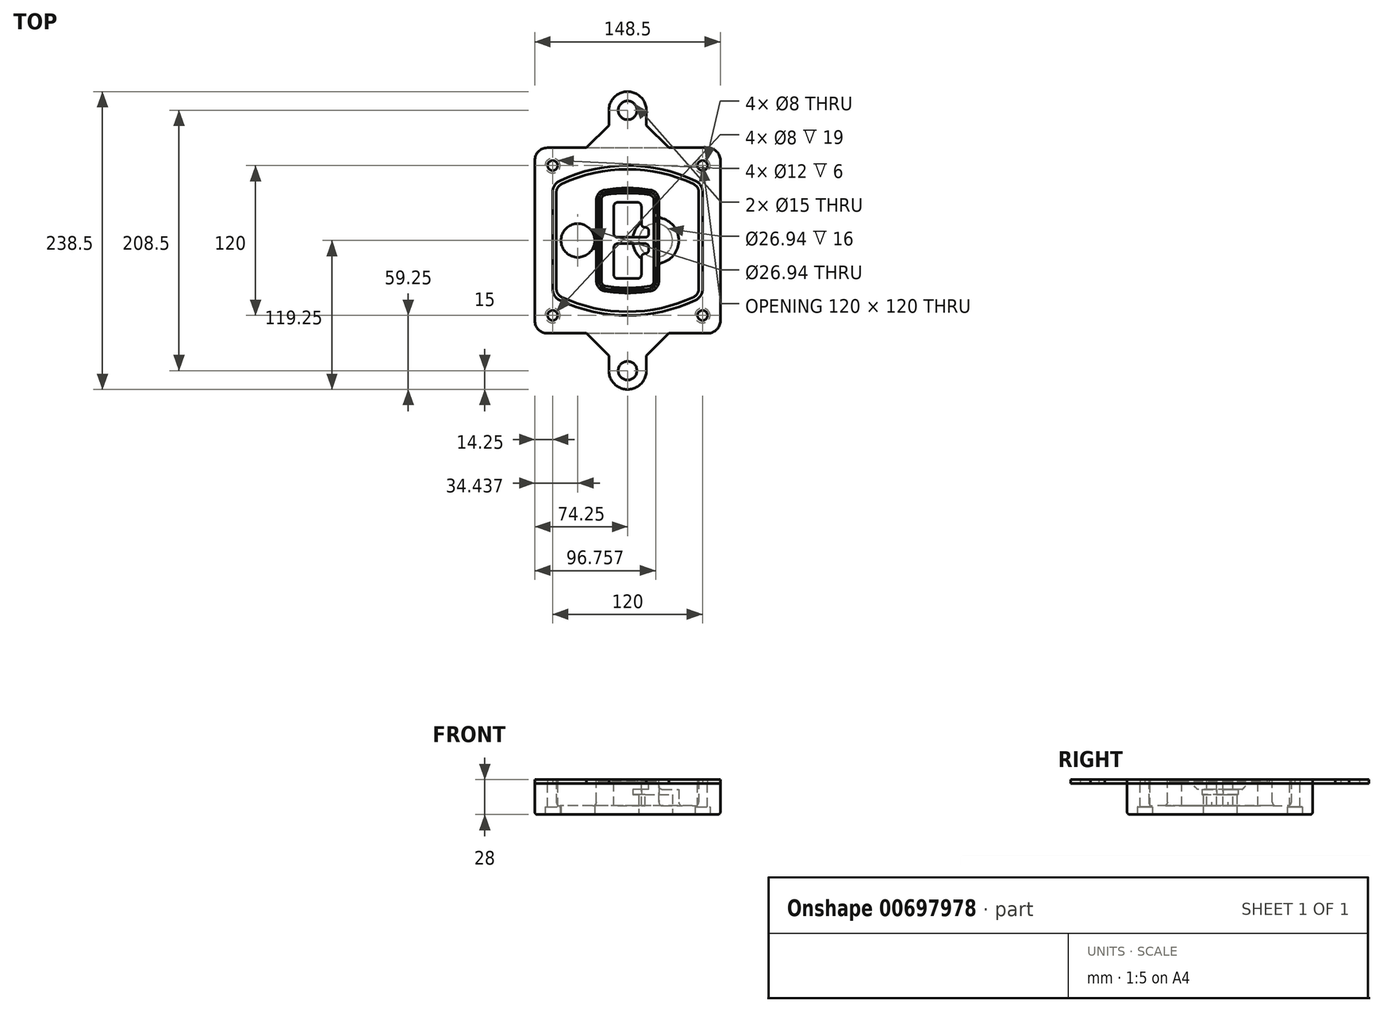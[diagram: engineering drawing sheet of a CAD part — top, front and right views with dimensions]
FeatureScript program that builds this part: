
annotation { "Feature Type Name" : "Feature", "Feature Type Description" : "" }
export const myFeature = defineFeature(function(context is Context, id is Id, definition is map)
    precondition{}
    {
        {
            var Q0;
            Q0=qCreatedBy(makeId("Top.planeOp"),FACE);
            var sketch = newSketch(context, id + "F0", { "sketchPlane" : qUnion([Q0])});
            skPoint(sketch, "E0.rect.middle", {"position": v(0, 0) * mm});
            skLineSegment(sketch, "E1.bottom", {"start": v(-64.25, -74.25) * mm, "end": v(64.25, -74.25) * mm});
            skLineSegment(sketch, "E1.top", {"start": v(-64.25, 74.25) * mm, "end": v(64.25, 74.25) * mm});
            skLineSegment(sketch, "E1.left", {"start": v(-74.25, -64.25) * mm, "end": v(-74.25, 64.25) * mm});
            skLineSegment(sketch, "E1.right", {"start": v(74.25, -64.25) * mm, "end": v(74.25, 64.25) * mm});
            skLineSegment(sketch, "E2", {"start": v(-74.25, 74.25) * mm, "end": v(74.25, -74.25) * mm, "construction": true});
            skLineSegment(sketch, "E3", {"start": v(74.25, 74.25) * mm, "end": v(-74.25, -74.25) * mm, "construction": true});
            skCircle(sketch, "E4", {"center": v(-60, 60) * mm, "radius": 4 * mm});
            skCircle(sketch, "E5", {"center": v(60, 60) * mm, "radius": 4 * mm});
            skCircle(sketch, "E6", {"center": v(60, -60) * mm, "radius": 4 * mm});
            skCircle(sketch, "E7", {"center": v(-60, -60) * mm, "radius": 4 * mm});
            skLineSegment(sketch, "E8", {"start": v(-60, 60) * mm, "end": v(60, 60) * mm, "construction": true});
            skLineSegment(sketch, "E9", {"start": v(60, 60) * mm, "end": v(60, -60) * mm, "construction": true});
            skLineSegment(sketch, "E10", {"start": v(60, -60) * mm, "end": v(-60, -60) * mm, "construction": true});
            skLineSegment(sketch, "E11", {"start": v(-60, -60) * mm, "end": v(-60, 60) * mm, "construction": true});
            skLineSegment(sketch, "E12", {"start": v(-60, 38.83) * mm, "end": v(-60, -38.83) * mm});
            skLineSegment(sketch, "E13", {"start": v(60, 38.83) * mm, "end": v(60, -38.83) * mm});
            skArc(sketch, "E14", {"start": v(54.26, 47.88) * mm, "mid": v(0, 60) * mm, "end": v(-54.26, 47.88) * mm});
            skArc(sketch, "E15", {"start": v(-54.26, -47.88) * mm, "mid": v(0, -60) * mm, "end": v(54.26, -47.88) * mm});
            skLineSegment(sketch, "E16", {"start": v(-60, 0) * mm, "end": v(60, 0) * mm, "construction": true});
            skPoint(sketch, "E17.visualSharp", {"position": v(-60, -45) * mm});
            skArc(sketch, "E17.filletArc", {"start": v(-60, -38.83) * mm, "mid": v(-58.44, -44.2) * mm, "end": v(-54.26, -47.88) * mm});
            skPoint(sketch, "E18.visualSharp", {"position": v(-60, 45) * mm});
            skArc(sketch, "E18.filletArc", {"start": v(-54.26, 47.88) * mm, "mid": v(-58.44, 44.2) * mm, "end": v(-60, 38.83) * mm});
            skPoint(sketch, "E19.visualSharp", {"position": v(60, 45) * mm});
            skArc(sketch, "E19.filletArc", {"start": v(60, 38.83) * mm, "mid": v(58.44, 44.2) * mm, "end": v(54.26, 47.88) * mm});
            skPoint(sketch, "E20.visualSharp", {"position": v(60, -45) * mm});
            skArc(sketch, "E20.filletArc", {"start": v(54.26, -47.88) * mm, "mid": v(58.44, -44.2) * mm, "end": v(60, -38.83) * mm});
            skPoint(sketch, "E21.visualSharp", {"position": v(-74.25, 74.25) * mm});
            skArc(sketch, "E21.filletArc", {"start": v(-64.25, 74.25) * mm, "mid": v(-71.32, 71.32) * mm, "end": v(-74.25, 64.25) * mm});
            skPoint(sketch, "E22.visualSharp", {"position": v(74.25, 74.25) * mm});
            skArc(sketch, "E22.filletArc", {"start": v(74.25, 64.25) * mm, "mid": v(71.32, 71.32) * mm, "end": v(64.25, 74.25) * mm});
            skPoint(sketch, "E23.visualSharp", {"position": v(74.25, -74.25) * mm});
            skArc(sketch, "E23.filletArc", {"start": v(64.25, -74.25) * mm, "mid": v(71.32, -71.32) * mm, "end": v(74.25, -64.25) * mm});
            skPoint(sketch, "E24.visualSharp", {"position": v(-74.25, -74.25) * mm});
            skArc(sketch, "E24.filletArc", {"start": v(-74.25, -64.25) * mm, "mid": v(-71.32, -71.32) * mm, "end": v(-64.25, -74.25) * mm});
            skArc(sketch, "E25.0", {"start": v(57, 38.83) * mm, "mid": v(55.9, 42.58) * mm, "end": v(52.98, 45.17) * mm});
            skLineSegment(sketch, "E25.1", {"start": v(57, 38.83) * mm, "end": v(57, -38.83) * mm});
            skArc(sketch, "E25.2", {"start": v(52.98, -45.17) * mm, "mid": v(55.9, -42.58) * mm, "end": v(57, -38.83) * mm});
            skArc(sketch, "E25.3", {"start": v(-52.98, -45.17) * mm, "mid": v(0, -57) * mm, "end": v(52.98, -45.17) * mm});
            skArc(sketch, "E25.4", {"start": v(-57, -38.83) * mm, "mid": v(-55.9, -42.58) * mm, "end": v(-52.98, -45.17) * mm});
            skArc(sketch, "E25.5", {"start": v(52.98, 45.17) * mm, "mid": v(0, 57) * mm, "end": v(-52.98, 45.17) * mm});
            skLineSegment(sketch, "E25.6", {"start": v(-57, 38.83) * mm, "end": v(-57, -38.83) * mm});
            skArc(sketch, "E25.7", {"start": v(-52.98, 45.17) * mm, "mid": v(-55.9, 42.58) * mm, "end": v(-57, 38.83) * mm});
            skArc(sketch, "E26.0", {"start": v(-55.96, 51.5) * mm, "mid": v(-61.82, 46.33) * mm, "end": v(-64, 38.83) * mm});
            skArc(sketch, "E26.1", {"start": v(55.96, 51.5) * mm, "mid": v(0, 64) * mm, "end": v(-55.96, 51.5) * mm});
            skArc(sketch, "E26.2", {"start": v(64, 38.83) * mm, "mid": v(61.82, 46.33) * mm, "end": v(55.96, 51.5) * mm});
            skLineSegment(sketch, "E26.3", {"start": v(64, 38.83) * mm, "end": v(64, -38.83) * mm});
            skArc(sketch, "E26.4", {"start": v(55.96, -51.5) * mm, "mid": v(61.82, -46.33) * mm, "end": v(64, -38.83) * mm});
            skLineSegment(sketch, "E26.5", {"start": v(-64, 38.83) * mm, "end": v(-64, -38.83) * mm});
            skArc(sketch, "E26.6", {"start": v(-55.96, -51.5) * mm, "mid": v(0, -64) * mm, "end": v(55.96, -51.5) * mm});
            skArc(sketch, "E26.7", {"start": v(-64, -38.83) * mm, "mid": v(-61.82, -46.33) * mm, "end": v(-55.96, -51.5) * mm});
            skSolve(sketch);
        }
        {
            var Q0;
            Q0=makeQuery(id+"F0.imprint","IMPRINT",FACE,{"disambiguationData":[TD([[makeQuery(id+"F0.imprint","IMPRINT",EDGE,{"derivedFrom":sQuery(id+"F0.wireOp",EDGE,"E1.bottom")}),1.0]])]});
            var Q1;
            Q1=makeQuery(id+"F0.imprint","IMPRINT",FACE,{"disambiguationData":[TD([[makeQuery(id+"F0.imprint","IMPRINT",EDGE,{"derivedFrom":sQuery(id+"F0.wireOp",EDGE,"E12")}),1.0]])]});
            var Q2;
            Q2=makeQuery(id+"F0.imprint","IMPRINT",FACE,{"disambiguationData":[TD([[makeQuery(id+"F0.imprint","IMPRINT",EDGE,{"derivedFrom":sQuery(id+"F0.wireOp",EDGE,"E25.0")}),1.0]])]});
            var Q3;
            Q3=makeQuery(id+"F0.imprint","IMPRINT",FACE,{"disambiguationData":[TD([[makeQuery(id+"F0.imprint","IMPRINT",EDGE,{"derivedFrom":sQuery(id+"F0.wireOp",EDGE,"E12")}),-1.0]])]});
            extrude(context, id + "F1", {"entities" : qUnion([Q0, Q1, Q2, Q3]), "oppositeDirection" : true, "depth" : 25 * mm});
        }
        {
            var Q0;
            Q0=makeQuery(id+"F0.imprint","IMPRINT",FACE,{"disambiguationData":[TD([[makeQuery(id+"F0.imprint","IMPRINT",EDGE,{"derivedFrom":sQuery(id+"F0.wireOp",EDGE,"E12")}),1.0]])]});
            extrude(context, id + "F2", {"entities" : qUnion([Q0]), "operationType" : NewBodyOperationType.ADD, "depth" : 3 * mm});
        }
        {
            var Q0;
            Q0=makeQuery(id+"F0.imprint","IMPRINT",FACE,{"disambiguationData":[TD([[makeQuery(id+"F0.imprint","IMPRINT",EDGE,{"derivedFrom":sQuery(id+"F0.wireOp",EDGE,"E25.0")}),1.0]])]});
            extrude(context, id + "F3", {"entities" : qUnion([Q0]), "operationType" : NewBodyOperationType.REMOVE, "oppositeDirection" : true, "depth" : 18 * mm});
        }
        {
            var Q0;
            Q0=makeQuery(id+"F2.opExtrude","CAP_FACE",FACE,{"disambiguationData":[OSD([sQuery(id+"F0.wireOp",EDGE,"E12"),sQuery(id+"F0.wireOp",EDGE,"E13"),sQuery(id+"F0.wireOp",EDGE,"E14"),sQuery(id+"F0.wireOp",EDGE,"E15"),sQuery(id+"F0.wireOp",EDGE,"E17.filletArc"),sQuery(id+"F0.wireOp",EDGE,"E18.filletArc"),sQuery(id+"F0.wireOp",EDGE,"E19.filletArc"),sQuery(id+"F0.wireOp",EDGE,"E20.filletArc"),sQuery(id+"F0.wireOp",EDGE,"E25.0"),sQuery(id+"F0.wireOp",EDGE,"E25.1"),sQuery(id+"F0.wireOp",EDGE,"E25.2"),sQuery(id+"F0.wireOp",EDGE,"E25.3"),sQuery(id+"F0.wireOp",EDGE,"E25.4"),sQuery(id+"F0.wireOp",EDGE,"E25.5"),sQuery(id+"F0.wireOp",EDGE,"E25.6"),sQuery(id+"F0.wireOp",EDGE,"E25.7")])],"isStart":false});
            var sketch = newSketch(context, id + "F4", { "sketchPlane" : qUnion([Q0])});
            skArc(sketch, "E27.0", {"start": v(-18.34, -40.45) * mm, "mid": v(0, -42) * mm, "end": v(18.34, -40.45) * mm});
            skArc(sketch, "E28.0", {"start": v(18.34, 40.45) * mm, "mid": v(0, 42) * mm, "end": v(-18.34, 40.45) * mm});
            skLineSegment(sketch, "E29", {"start": v(-25, 32.57) * mm, "end": v(-25, -32.57) * mm});
            skLineSegment(sketch, "E30", {"start": v(25, 32.57) * mm, "end": v(25, -32.57) * mm});
            skLineSegment(sketch, "E31", {"start": v(-25, 39.1) * mm, "end": v(25, 39.1) * mm, "construction": true});
            skLineSegment(sketch, "E32", {"start": v(-25, -39.1) * mm, "end": v(25, -39.1) * mm, "construction": true});
            skPoint(sketch, "E33.visualSharp", {"position": v(-25, 39.1) * mm});
            skArc(sketch, "E33.filletArc", {"start": v(-18.34, 40.45) * mm, "mid": v(-23.11, 37.73) * mm, "end": v(-25, 32.57) * mm});
            skPoint(sketch, "E34.visualSharp", {"position": v(25, 39.1) * mm});
            skArc(sketch, "E34.filletArc", {"start": v(25, 32.57) * mm, "mid": v(23.11, 37.73) * mm, "end": v(18.34, 40.45) * mm});
            skPoint(sketch, "E35.visualSharp", {"position": v(25, -39.1) * mm});
            skArc(sketch, "E35.filletArc", {"start": v(18.34, -40.45) * mm, "mid": v(23.11, -37.73) * mm, "end": v(25, -32.57) * mm});
            skPoint(sketch, "E36.visualSharp", {"position": v(-25, -39.1) * mm});
            skArc(sketch, "E36.filletArc", {"start": v(-25, -32.57) * mm, "mid": v(-23.11, -37.73) * mm, "end": v(-18.34, -40.45) * mm});
            skArc(sketch, "E37.0", {"start": v(52.98, 45.17) * mm, "mid": v(0, 57) * mm, "end": v(-52.98, 45.17) * mm});
            skArc(sketch, "E37.1", {"start": v(-52.98, 45.17) * mm, "mid": v(-55.9, 42.58) * mm, "end": v(-57, 38.83) * mm});
            skLineSegment(sketch, "E37.2", {"start": v(-57, 38.83) * mm, "end": v(-57, -38.83) * mm});
            skArc(sketch, "E37.3", {"start": v(-57, -38.83) * mm, "mid": v(-55.9, -42.58) * mm, "end": v(-52.98, -45.17) * mm});
            skArc(sketch, "E37.4", {"start": v(-52.98, -45.17) * mm, "mid": v(0, -57) * mm, "end": v(52.98, -45.17) * mm});
            skArc(sketch, "E37.5", {"start": v(52.98, -45.17) * mm, "mid": v(55.9, -42.58) * mm, "end": v(57, -38.83) * mm});
            skLineSegment(sketch, "E37.6", {"start": v(57, 38.83) * mm, "end": v(57, -38.83) * mm});
            skArc(sketch, "E37.7", {"start": v(57, 38.83) * mm, "mid": v(55.9, 42.58) * mm, "end": v(52.98, 45.17) * mm});
            skLineSegment(sketch, "E38.0", {"start": v(23, 32.57) * mm, "end": v(23, -32.57) * mm});
            skArc(sketch, "E38.1", {"start": v(18, -38.48) * mm, "mid": v(21.58, -36.44) * mm, "end": v(23, -32.57) * mm});
            skArc(sketch, "E38.2", {"start": v(-18, -38.48) * mm, "mid": v(0, -40) * mm, "end": v(18, -38.48) * mm});
            skArc(sketch, "E38.3", {"start": v(-23, -32.57) * mm, "mid": v(-21.58, -36.44) * mm, "end": v(-18, -38.48) * mm});
            skLineSegment(sketch, "E38.4", {"start": v(-23, 32.57) * mm, "end": v(-23, -32.57) * mm});
            skArc(sketch, "E38.5", {"start": v(23, 32.57) * mm, "mid": v(21.58, 36.44) * mm, "end": v(18, 38.48) * mm});
            skArc(sketch, "E38.6", {"start": v(-18, 38.48) * mm, "mid": v(-21.58, 36.44) * mm, "end": v(-23, 32.57) * mm});
            skArc(sketch, "E38.7", {"start": v(18, 38.48) * mm, "mid": v(0, 40) * mm, "end": v(-18, 38.48) * mm});
            skArc(sketch, "E39.0", {"start": v(21, 32.57) * mm, "mid": v(20.06, 35.15) * mm, "end": v(17.67, 36.5) * mm});
            skLineSegment(sketch, "E39.1", {"start": v(21, 32.57) * mm, "end": v(21, -32.57) * mm});
            skArc(sketch, "E39.2", {"start": v(17.67, -36.5) * mm, "mid": v(20.06, -35.15) * mm, "end": v(21, -32.57) * mm});
            skArc(sketch, "E39.3", {"start": v(-17.67, -36.5) * mm, "mid": v(0, -38) * mm, "end": v(17.67, -36.5) * mm});
            skArc(sketch, "E39.4", {"start": v(-21, -32.57) * mm, "mid": v(-20.06, -35.15) * mm, "end": v(-17.67, -36.5) * mm});
            skArc(sketch, "E39.5", {"start": v(17.67, 36.5) * mm, "mid": v(0, 38) * mm, "end": v(-17.67, 36.5) * mm});
            skLineSegment(sketch, "E39.6", {"start": v(-21, 32.57) * mm, "end": v(-21, -32.57) * mm});
            skArc(sketch, "E39.7", {"start": v(-17.67, 36.5) * mm, "mid": v(-20.06, 35.15) * mm, "end": v(-21, 32.57) * mm});
            skLineSegment(sketch, "E40", {"start": v(-25, 0) * mm, "end": v(25, 0) * mm, "construction": true});
            skLineSegment(sketch, "E41", {"start": v(-11, 5.5) * mm, "end": v(-11, 27.5) * mm});
            skLineSegment(sketch, "E42", {"start": v(-8, 30.5) * mm, "end": v(8, 30.5) * mm});
            skLineSegment(sketch, "E43", {"start": v(11, 27.5) * mm, "end": v(11, 13.5) * mm});
            skLineSegment(sketch, "E44", {"start": v(14, 10.5) * mm, "end": v(14, 10.5) * mm});
            skLineSegment(sketch, "E45", {"start": v(17, 7.5) * mm, "end": v(17, 5.5) * mm});
            skLineSegment(sketch, "E46", {"start": v(14, 2.5) * mm, "end": v(-8, 2.5) * mm});
            skPoint(sketch, "E47.visualSharp", {"position": v(-11, 30.5) * mm});
            skArc(sketch, "E47.filletArc", {"start": v(-8, 30.5) * mm, "mid": v(-10.12, 29.62) * mm, "end": v(-11, 27.5) * mm});
            skPoint(sketch, "E48.visualSharp", {"position": v(11, 30.5) * mm});
            skArc(sketch, "E48.filletArc", {"start": v(11, 27.5) * mm, "mid": v(10.12, 29.62) * mm, "end": v(8, 30.5) * mm});
            skPoint(sketch, "E49.visualSharp", {"position": v(11, 10.5) * mm});
            skArc(sketch, "E49.filletArc", {"start": v(11, 13.5) * mm, "mid": v(11.88, 11.38) * mm, "end": v(14, 10.5) * mm});
            skPoint(sketch, "E50.visualSharp", {"position": v(17, 10.5) * mm});
            skArc(sketch, "E50.filletArc", {"start": v(17, 7.5) * mm, "mid": v(16.12, 9.62) * mm, "end": v(14, 10.5) * mm});
            skPoint(sketch, "E51.visualSharp", {"position": v(17, 2.5) * mm});
            skArc(sketch, "E51.filletArc", {"start": v(14, 2.5) * mm, "mid": v(16.12, 3.38) * mm, "end": v(17, 5.5) * mm});
            skPoint(sketch, "E52.visualSharp", {"position": v(-11, 2.5) * mm});
            skArc(sketch, "E52.filletArc", {"start": v(-11, 5.5) * mm, "mid": v(-10.12, 3.38) * mm, "end": v(-8, 2.5) * mm});
            skLineSegment(sketch, "E53.0.MirrorCS", {"start": v(14, -2.5) * mm, "end": v(-8, -2.5) * mm});
            skArc(sketch, "E54.0.MirrorCS", {"start": v(-11, -5.5) * mm, "mid": v(-10.12, -3.38) * mm, "end": v(-8, -2.5) * mm});
            skLineSegment(sketch, "E55.0.MirrorCS", {"start": v(-11, -5.5) * mm, "end": v(-11, -27.5) * mm});
            skArc(sketch, "E56.0.MirrorCS", {"start": v(-8, -30.5) * mm, "mid": v(-10.12, -29.62) * mm, "end": v(-11, -27.5) * mm});
            skLineSegment(sketch, "E57.0.MirrorCS", {"start": v(-8, -30.5) * mm, "end": v(8, -30.5) * mm});
            skArc(sketch, "E58.0.MirrorCS", {"start": v(11, -27.5) * mm, "mid": v(10.12, -29.62) * mm, "end": v(8, -30.5) * mm});
            skLineSegment(sketch, "E59.0.MirrorCS", {"start": v(11, -27.5) * mm, "end": v(11, -13.5) * mm});
            skArc(sketch, "E60.0.MirrorCS", {"start": v(11, -13.5) * mm, "mid": v(11.88, -11.38) * mm, "end": v(14, -10.5) * mm});
            skArc(sketch, "E61.0.MirrorCS", {"start": v(17, -7.5) * mm, "mid": v(16.12, -9.62) * mm, "end": v(14, -10.5) * mm});
            skLineSegment(sketch, "E62.0.MirrorCS", {"start": v(17, -7.5) * mm, "end": v(17, -5.5) * mm});
            skArc(sketch, "E63.0.MirrorCS", {"start": v(14, -2.5) * mm, "mid": v(16.12, -3.38) * mm, "end": v(17, -5.5) * mm});
            skSolve(sketch);
        }
        {
            var Q0;
            Q0=makeQuery(id+"F4.imprint","IMPRINT",FACE,{"disambiguationData":[TD([[makeQuery(id+"F4.imprint","IMPRINT",EDGE,{"derivedFrom":sQuery(id+"F4.wireOp",EDGE,"E27.0")}),1.0]])]});
            var Q1;
            Q1=makeQuery(id+"F4.imprint","IMPRINT",FACE,{"disambiguationData":[TD([[makeQuery(id+"F4.imprint","IMPRINT",EDGE,{"derivedFrom":sQuery(id+"F4.wireOp",EDGE,"E38.0")}),-1.0]])]});
            var Q2;
            Q2=makeQuery(id+"F4.imprint","IMPRINT",FACE,{"disambiguationData":[TD([[makeQuery(id+"F4.imprint","IMPRINT",EDGE,{"derivedFrom":sQuery(id+"F4.wireOp",EDGE,"E39.0")}),1.0]])]});
            extrude(context, id + "F5", {"entities" : qUnion([Q0, Q1, Q2]), "operationType" : NewBodyOperationType.ADD, "endBound" : BoundingType.UP_TO_NEXT, "oppositeDirection" : true, "depth" : 25 * mm});
        }
        {
            var Q0;
            Q0=makeQuery(id+"F4.imprint","IMPRINT",FACE,{"disambiguationData":[TD([[makeQuery(id+"F4.imprint","IMPRINT",EDGE,{"derivedFrom":sQuery(id+"F4.wireOp",EDGE,"E38.0")}),-1.0]])]});
            extrude(context, id + "F6", {"entities" : qUnion([Q0]), "operationType" : NewBodyOperationType.REMOVE, "oppositeDirection" : true, "depth" : 2 * mm});
        }
        {
            var Q0;
            Q0=makeQuery(id+"F1.opExtrude","CAP_FACE",FACE,{"disambiguationData":[OSD([sQuery(id+"F0.wireOp",EDGE,"E1.bottom"),sQuery(id+"F0.wireOp",EDGE,"E1.top"),sQuery(id+"F0.wireOp",EDGE,"E1.left"),sQuery(id+"F0.wireOp",EDGE,"E1.right"),sQuery(id+"F0.wireOp",EDGE,"E4"),sQuery(id+"F0.wireOp",EDGE,"E5"),sQuery(id+"F0.wireOp",EDGE,"E6"),sQuery(id+"F0.wireOp",EDGE,"E7"),sQuery(id+"F0.wireOp",EDGE,"E21.filletArc"),sQuery(id+"F0.wireOp",EDGE,"E22.filletArc"),sQuery(id+"F0.wireOp",EDGE,"E23.filletArc"),sQuery(id+"F0.wireOp",EDGE,"E24.filletArc")])],"isStart":false});
            var sketch = newSketch(context, id + "F7", { "sketchPlane" : qUnion([Q0])});
            skCircle(sketch, "E64", {"center": v(22.5, 0) * mm, "radius": 13.47 * mm});
            skCircle(sketch, "E65", {"center": v(-39.81, 0) * mm, "radius": 13.47 * mm});
            skLineSegment(sketch, "E66", {"start": v(74.25, 0) * mm, "end": v(-74.25, 0) * mm});
            skCircle(sketch, "E67", {"center": v(22.5, 0) * mm, "radius": 18.47 * mm});
            skCircle(sketch, "E68", {"center": v(60, -60) * mm, "radius": 6 * mm});
            skCircle(sketch, "E69", {"center": v(-60, -60) * mm, "radius": 6 * mm});
            skCircle(sketch, "E70", {"center": v(-60, 60) * mm, "radius": 6 * mm});
            skCircle(sketch, "E71", {"center": v(60, 60) * mm, "radius": 6 * mm});
            skSolve(sketch);
        }
        {
            var Q0;
            {var subQ1=sQuery(id+"F7.wireOp",EDGE,"E66");var subQ4=sQuery(id+"F7.wireOp",EDGE,"E64");var subQ6=makeQuery(id+"F7.imprint","INTERSECT",VERTEX,{"disambiguationData":[OD(0.0)],"derivedFrom":[subQ4,subQ1]});Q0=makeQuery(id+"F7.imprint","IMPRINT",FACE,{"disambiguationData":[TD([[makeQuery(id+"F7.imprint","IMPRINT",EDGE,{"disambiguationData":[TD([[subQ6,-1.0]])],"derivedFrom":subQ4}),-1.0]])]});}
            var Q1;
            {var subQ0=sQuery(id+"F7.wireOp",EDGE,"E66");var subQ1=sQuery(id+"F7.wireOp",EDGE,"E64");var subQ3=makeQuery(id+"F7.imprint","INTERSECT",VERTEX,{"disambiguationData":[OD(0.0)],"derivedFrom":[subQ1,subQ0]});Q1=makeQuery(id+"F7.imprint","IMPRINT",FACE,{"disambiguationData":[TD([[makeQuery(id+"F7.imprint","IMPRINT",EDGE,{"disambiguationData":[TD([[subQ3,-1.0]])],"derivedFrom":subQ1}),1.0]])]});}
            var Q2;
            {var subQ0=sQuery(id+"F7.wireOp",EDGE,"E66");var subQ1=sQuery(id+"F7.wireOp",EDGE,"E64");var subQ3=makeQuery(id+"F7.imprint","INTERSECT",VERTEX,{"disambiguationData":[OD(0.0)],"derivedFrom":[subQ1,subQ0]});Q2=makeQuery(id+"F7.imprint","IMPRINT",FACE,{"disambiguationData":[TD([[makeQuery(id+"F7.imprint","IMPRINT",EDGE,{"disambiguationData":[TD([[subQ3,1.0]])],"derivedFrom":subQ1}),1.0]])]});}
            var Q3;
            {var subQ1=sQuery(id+"F7.wireOp",EDGE,"E66");var subQ4=sQuery(id+"F7.wireOp",EDGE,"E64");var subQ6=makeQuery(id+"F7.imprint","INTERSECT",VERTEX,{"disambiguationData":[OD(0.0)],"derivedFrom":[subQ4,subQ1]});Q3=makeQuery(id+"F7.imprint","IMPRINT",FACE,{"disambiguationData":[TD([[makeQuery(id+"F7.imprint","IMPRINT",EDGE,{"disambiguationData":[TD([[subQ6,1.0]])],"derivedFrom":subQ4}),-1.0]])]});}
            extrude(context, id + "F8", {"entities" : qUnion([Q0, Q1, Q2, Q3]), "operationType" : NewBodyOperationType.ADD, "oppositeDirection" : true, "depth" : 20 * mm});
        }
        {
            var Q0;
            {var subQ0=sQuery(id+"F7.wireOp",EDGE,"E66");var subQ1=sQuery(id+"F7.wireOp",EDGE,"E64");var subQ3=makeQuery(id+"F7.imprint","INTERSECT",VERTEX,{"disambiguationData":[OD(0.0)],"derivedFrom":[subQ1,subQ0]});Q0=makeQuery(id+"F7.imprint","IMPRINT",FACE,{"disambiguationData":[TD([[makeQuery(id+"F7.imprint","IMPRINT",EDGE,{"disambiguationData":[TD([[subQ3,-1.0]])],"derivedFrom":subQ1}),1.0]])]});}
            var Q1;
            {var subQ0=sQuery(id+"F7.wireOp",EDGE,"E66");var subQ1=sQuery(id+"F7.wireOp",EDGE,"E64");var subQ3=makeQuery(id+"F7.imprint","INTERSECT",VERTEX,{"disambiguationData":[OD(0.0)],"derivedFrom":[subQ1,subQ0]});Q1=makeQuery(id+"F7.imprint","IMPRINT",FACE,{"disambiguationData":[TD([[makeQuery(id+"F7.imprint","IMPRINT",EDGE,{"disambiguationData":[TD([[subQ3,1.0]])],"derivedFrom":subQ1}),1.0]])]});}
            extrude(context, id + "F9", {"entities" : qUnion([Q0, Q1]), "operationType" : NewBodyOperationType.REMOVE, "oppositeDirection" : true, "depth" : 16 * mm});
        }
        {
            var Q0;
            {var subQ0=sQuery(id+"F7.wireOp",EDGE,"E66");var subQ1=sQuery(id+"F7.wireOp",EDGE,"E65");var subQ3=makeQuery(id+"F7.imprint","INTERSECT",VERTEX,{"disambiguationData":[OD(0.0)],"derivedFrom":[subQ1,subQ0]});Q0=makeQuery(id+"F7.imprint","IMPRINT",FACE,{"disambiguationData":[TD([[makeQuery(id+"F7.imprint","IMPRINT",EDGE,{"disambiguationData":[TD([[subQ3,-1.0]])],"derivedFrom":subQ1}),1.0]])]});}
            var Q1;
            {var subQ0=sQuery(id+"F7.wireOp",EDGE,"E66");var subQ1=sQuery(id+"F7.wireOp",EDGE,"E65");var subQ3=makeQuery(id+"F7.imprint","INTERSECT",VERTEX,{"disambiguationData":[OD(0.0)],"derivedFrom":[subQ1,subQ0]});Q1=makeQuery(id+"F7.imprint","IMPRINT",FACE,{"disambiguationData":[TD([[makeQuery(id+"F7.imprint","IMPRINT",EDGE,{"disambiguationData":[TD([[subQ3,1.0]])],"derivedFrom":subQ1}),1.0]])]});}
            extrude(context, id + "F10", {"entities" : qUnion([Q0, Q1]), "operationType" : NewBodyOperationType.REMOVE, "oppositeDirection" : true, "depth" : 25 * mm});
        }
        {
            var Q0;
            Q0=makeQuery(id+"F7.imprint","IMPRINT",FACE,{"disambiguationData":[TD([[makeQuery(id+"F7.imprint","IMPRINT",EDGE,{"derivedFrom":sQuery(id+"F7.wireOp",EDGE,"E68")}),1.0]])]});
            var Q1;
            Q1=makeQuery(id+"F7.imprint","IMPRINT",FACE,{"disambiguationData":[TD([[makeQuery(id+"F7.imprint","IMPRINT",EDGE,{"derivedFrom":makeQuery(id+"F1.opExtrude","CAP_EDGE",EDGE,{"disambiguationData":[OSD([sQuery(id+"F0.wireOp",EDGE,"E5")])],"isStart":false})}),-1.0]])]});
            var Q2;
            Q2=makeQuery(id+"F7.imprint","IMPRINT",FACE,{"disambiguationData":[TD([[makeQuery(id+"F7.imprint","IMPRINT",EDGE,{"derivedFrom":sQuery(id+"F7.wireOp",EDGE,"E69")}),1.0]])]});
            var Q3;
            Q3=makeQuery(id+"F7.imprint","IMPRINT",FACE,{"disambiguationData":[TD([[makeQuery(id+"F7.imprint","IMPRINT",EDGE,{"derivedFrom":makeQuery(id+"F1.opExtrude","CAP_EDGE",EDGE,{"disambiguationData":[OSD([sQuery(id+"F0.wireOp",EDGE,"E4")])],"isStart":false})}),-1.0]])]});
            var Q4;
            Q4=makeQuery(id+"F7.imprint","IMPRINT",FACE,{"disambiguationData":[TD([[makeQuery(id+"F7.imprint","IMPRINT",EDGE,{"derivedFrom":sQuery(id+"F7.wireOp",EDGE,"E70")}),1.0]])]});
            var Q5;
            Q5=makeQuery(id+"F7.imprint","IMPRINT",FACE,{"disambiguationData":[TD([[makeQuery(id+"F7.imprint","IMPRINT",EDGE,{"derivedFrom":makeQuery(id+"F1.opExtrude","CAP_EDGE",EDGE,{"disambiguationData":[OSD([sQuery(id+"F0.wireOp",EDGE,"E7")])],"isStart":false})}),-1.0]])]});
            var Q6;
            Q6=makeQuery(id+"F7.imprint","IMPRINT",FACE,{"disambiguationData":[TD([[makeQuery(id+"F7.imprint","IMPRINT",EDGE,{"derivedFrom":sQuery(id+"F7.wireOp",EDGE,"E71")}),1.0]])]});
            var Q7;
            Q7=makeQuery(id+"F7.imprint","IMPRINT",FACE,{"disambiguationData":[TD([[makeQuery(id+"F7.imprint","IMPRINT",EDGE,{"derivedFrom":makeQuery(id+"F1.opExtrude","CAP_EDGE",EDGE,{"disambiguationData":[OSD([sQuery(id+"F0.wireOp",EDGE,"E6")])],"isStart":false})}),-1.0]])]});
            extrude(context, id + "F11", {"entities" : qUnion([Q0, Q1, Q2, Q3, Q4, Q5, Q6, Q7]), "operationType" : NewBodyOperationType.REMOVE, "oppositeDirection" : true, "depth" : 6 * mm});
        }
        {
            var Q0;
            Q0=makeQuery(id+"F9.boolean.opBoolean","COPY",FACE,{"derivedFrom":makeQuery(id+"F9.opExtrude","CAP_FACE",FACE,{"disambiguationData":[OSD([sQuery(id+"F7.wireOp",EDGE,"E64")])],"isStart":false})});
            var sketch = newSketch(context, id + "F12", { "sketchPlane" : qUnion([Q0])});
            skArc(sketch, "E72.0", {"start": v(11, 14.45) * mm, "mid": v(6.45, 9.13) * mm, "end": v(4.2, 2.5) * mm});
            skArc(sketch, "E72.1", {"start": v(4.2, -2.5) * mm, "mid": v(6.45, -9.13) * mm, "end": v(11, -14.45) * mm});
            skLineSegment(sketch, "E73", {"start": v(4.2, -2.5) * mm, "end": v(14, -2.5) * mm});
            skLineSegment(sketch, "E74.0", {"start": v(14, 2.5) * mm, "end": v(4.2, 2.5) * mm});
            skArc(sketch, "E74.1", {"start": v(14, 2.5) * mm, "mid": v(16.12, 3.38) * mm, "end": v(17, 5.5) * mm});
            skLineSegment(sketch, "E74.2", {"start": v(17, 7.5) * mm, "end": v(17, 5.5) * mm});
            skArc(sketch, "E74.3", {"start": v(17, 7.5) * mm, "mid": v(16.12, 9.62) * mm, "end": v(14, 10.5) * mm});
            skArc(sketch, "E74.4", {"start": v(11, 13.5) * mm, "mid": v(11.88, 11.38) * mm, "end": v(14, 10.5) * mm});
            skLineSegment(sketch, "E74.5", {"start": v(11, 14.45) * mm, "end": v(11, 13.5) * mm});
            skLineSegment(sketch, "E74.7", {"start": v(14, -2.5) * mm, "end": v(4.2, -2.5) * mm});
            skArc(sketch, "E74.8", {"start": v(14, -2.5) * mm, "mid": v(16.12, -3.38) * mm, "end": v(17, -5.5) * mm});
            skLineSegment(sketch, "E74.9", {"start": v(17, -7.5) * mm, "end": v(17, -5.5) * mm});
            skArc(sketch, "E74.10", {"start": v(17, -7.5) * mm, "mid": v(16.12, -9.62) * mm, "end": v(14, -10.5) * mm});
            skArc(sketch, "E74.11", {"start": v(11, -13.5) * mm, "mid": v(11.88, -11.38) * mm, "end": v(14, -10.5) * mm});
            skLineSegment(sketch, "E74.12", {"start": v(11, -14.45) * mm, "end": v(11, -13.5) * mm});
            skPoint(sketch, "E75.orphan", {"position": v(11, -27.5) * mm});
            skPoint(sketch, "E76.orphan", {"position": v(-8, -2.5) * mm});
            skPoint(sketch, "E77.orphan", {"position": v(-8, 2.5) * mm});
            skPoint(sketch, "E78.orphan", {"position": v(11, 27.5) * mm});
            skSolve(sketch);
        }
        {
            var Q0;
            {var subQ7=sQuery(id+"F12.wireOp",EDGE,"E72.0");var subQ14=sQuery(id+"F12.wireOp",EDGE,"E72.1");var subQ16=sQuery(id+"F12.wireOp",EDGE,"E74.1");var subQ18=sQuery(id+"F12.wireOp",EDGE,"E74.8");Q0=qUnion([makeQuery(id+"F12.imprint","IMPRINT",FACE,{"disambiguationData":[TD([[makeQuery(id+"F12.imprint","IMPRINT",EDGE,{"derivedFrom":subQ7}),1.0]])]}),makeQuery(id+"F12.imprint","IMPRINT",FACE,{"disambiguationData":[TD([[makeQuery(id+"F12.imprint","IMPRINT",EDGE,{"derivedFrom":subQ14}),1.0]])]}),makeQuery(id+"F12.imprint","IMPRINT",FACE,{"disambiguationData":[TD([[makeQuery(id+"F12.imprint","IMPRINT",EDGE,{"derivedFrom":subQ16}),1.0]])]}),makeQuery(id+"F12.imprint","IMPRINT",FACE,{"disambiguationData":[TD([[makeQuery(id+"F12.imprint","IMPRINT",EDGE,{"derivedFrom":subQ18}),-1.0]])]})]);}
            var Q1;
            Q1=makeQuery(id+"F5.boolean.opBoolean","SPLIT",FACE,{"disambiguationData":[TD([makeQuery(id+"F5.opExtrude","SWEPT_FACE",FACE,{"disambiguationData":[OSD([sQuery(id+"F4.wireOp",EDGE,"E41")])]})])],"derivedFrom":makeQuery(id+"F3.boolean.opBoolean","COPY",FACE,{"derivedFrom":makeQuery(id+"F3.opExtrude","CAP_FACE",FACE,{"disambiguationData":[OSD([sQuery(id+"F0.wireOp",EDGE,"E25.0"),sQuery(id+"F0.wireOp",EDGE,"E25.1"),sQuery(id+"F0.wireOp",EDGE,"E25.2"),sQuery(id+"F0.wireOp",EDGE,"E25.3"),sQuery(id+"F0.wireOp",EDGE,"E25.4"),sQuery(id+"F0.wireOp",EDGE,"E25.5"),sQuery(id+"F0.wireOp",EDGE,"E25.6"),sQuery(id+"F0.wireOp",EDGE,"E25.7")])],"isStart":false})})});
            extrude(context, id + "F13", {"entities" : qUnion([Q0]), "operationType" : NewBodyOperationType.REMOVE, "endBound" : BoundingType.UP_TO_SURFACE, "endBoundEntityFace" : qUnion([Q1]), "depth" : 25 * mm});
        }
        {
            var Q0;
            Q0=makeQuery(id+"F3.boolean.opBoolean","COPY",EDGE,{"derivedFrom":makeQuery(id+"F3.opExtrude","CAP_EDGE",EDGE,{"disambiguationData":[OSD([sQuery(id+"F0.wireOp",EDGE,"E25.6")])],"isStart":false})});
            var Q1;
            Q1=makeQuery(id+"F8.boolean.opBoolean","INTERSECT",EDGE,{"derivedFrom":[makeQuery(id+"F5.opExtrude","SWEPT_FACE",FACE,{"disambiguationData":[OSD([sQuery(id+"F4.wireOp",EDGE,"E30")])]}),makeQuery(id+"F8.opExtrude","CAP_FACE",FACE,{"disambiguationData":[OSD([sQuery(id+"F7.wireOp",EDGE,"E67")])],"isStart":false})]});
            var Q2;
            Q2=makeQuery(id+"F8.boolean.opBoolean","INTERSECT",EDGE,{"disambiguationData":[OD(1.0)],"derivedFrom":[makeQuery(id+"F5.opExtrude","SWEPT_FACE",FACE,{"disambiguationData":[OSD([sQuery(id+"F4.wireOp",EDGE,"E30")])]}),makeQuery(id+"F8.opExtrude","SWEPT_FACE",FACE,{"disambiguationData":[OSD([sQuery(id+"F7.wireOp",EDGE,"E67")])]})]});
            var Q3;
            {var subQ0=sQuery(id+"F4.wireOp",EDGE,"E30");Q3=makeQuery(id+"F8.boolean.opBoolean","SPLIT",EDGE,{"disambiguationData":[TD([makeQuery(id+"F5.opExtrude","SWEPT_FACE",FACE,{"disambiguationData":[OSD([sQuery(id+"F4.wireOp",EDGE,"E35.filletArc")])]})])],"derivedFrom":makeQuery(id+"F5.opExtrude","CAP_EDGE",EDGE,{"disambiguationData":[OSD([subQ0])],"isStart":false})});}
            var Q4;
            {var subQ0=sQuery(id+"F0.wireOp",EDGE,"E25.7");var subQ1=sQuery(id+"F0.wireOp",EDGE,"E25.1");var subQ2=sQuery(id+"F0.wireOp",EDGE,"E25.6");var subQ3=sQuery(id+"F0.wireOp",EDGE,"E25.5");var subQ4=sQuery(id+"F0.wireOp",EDGE,"E25.4");var subQ5=sQuery(id+"F0.wireOp",EDGE,"E25.0");var subQ6=sQuery(id+"F0.wireOp",EDGE,"E25.2");var subQ7=sQuery(id+"F0.wireOp",EDGE,"E25.3");Q4=makeQuery(id+"F8.boolean.opBoolean","INTERSECT",EDGE,{"derivedFrom":[makeQuery(id+"F5.boolean.opBoolean","SPLIT",FACE,{"disambiguationData":[TD([makeQuery(id+"F2.opExtrude","SWEPT_FACE",FACE,{"disambiguationData":[OSD([subQ5])]})])],"derivedFrom":makeQuery(id+"F3.boolean.opBoolean","COPY",FACE,{"derivedFrom":makeQuery(id+"F3.opExtrude","CAP_FACE",FACE,{"disambiguationData":[OSD([subQ5,subQ1,subQ6,subQ7,subQ4,subQ3,subQ2,subQ0])],"isStart":false})})}),makeQuery(id+"F8.opExtrude","SWEPT_FACE",FACE,{"disambiguationData":[OSD([sQuery(id+"F7.wireOp",EDGE,"E67")])]})]});}
            var Q5;
            Q5=makeQuery(id+"F8.boolean.opBoolean","INTERSECT",EDGE,{"disambiguationData":[OD(0.0)],"derivedFrom":[makeQuery(id+"F5.opExtrude","SWEPT_FACE",FACE,{"disambiguationData":[OSD([sQuery(id+"F4.wireOp",EDGE,"E30")])]}),makeQuery(id+"F8.opExtrude","SWEPT_FACE",FACE,{"disambiguationData":[OSD([sQuery(id+"F7.wireOp",EDGE,"E67")])]})]});
            fillet(context, id + "F14", {"entities" : qUnion([Q0, Q1, Q2, Q3, Q4, Q5]), "radius" : 3 * mm, "tangentPropagation" : true, "allowEdgeOverflow" : false});
        }
        {
            var Q0;
            Q0=makeQuery(id+"F1.opExtrude","CAP_EDGE",EDGE,{"disambiguationData":[OSD([sQuery(id+"F0.wireOp",EDGE,"E1.bottom")])],"isStart":false});
            fillet(context, id + "F15", {"entities" : qUnion([Q0]), "radius" : 2 * mm, "tangentPropagation" : true, "allowEdgeOverflow" : false});
        }
        {
            var Q0;
            {var subQ0=sQuery(id+"F0.wireOp",EDGE,"E21.filletArc");var subQ1=sQuery(id+"F0.wireOp",EDGE,"E7");var subQ2=sQuery(id+"F0.wireOp",EDGE,"E6");var subQ3=sQuery(id+"F0.wireOp",EDGE,"E5");var subQ4=sQuery(id+"F0.wireOp",EDGE,"E4");var subQ5=sQuery(id+"F0.wireOp",EDGE,"E22.filletArc");var subQ6=sQuery(id+"F0.wireOp",EDGE,"E1.bottom");var subQ7=sQuery(id+"F0.wireOp",EDGE,"E1.right");var subQ8=sQuery(id+"F0.wireOp",EDGE,"E1.top");var subQ9=sQuery(id+"F0.wireOp",EDGE,"E1.left");var subQ10=sQuery(id+"F0.wireOp",EDGE,"E23.filletArc");var subQ11=sQuery(id+"F0.wireOp",EDGE,"E24.filletArc");Q0=makeQuery(id+"F2.boolean.opBoolean","SPLIT",FACE,{"disambiguationData":[TD([makeQuery(id+"F1.opExtrude","SWEPT_FACE",FACE,{"disambiguationData":[OSD([subQ6])]})])],"derivedFrom":makeQuery(id+"F1.opExtrude","CAP_FACE",FACE,{"disambiguationData":[OSD([subQ6,subQ8,subQ9,subQ7,subQ4,subQ3,subQ2,subQ1,subQ0,subQ5,subQ10,subQ11])],"isStart":true})});}
            var sketch = newSketch(context, id + "F16", { "sketchPlane" : qUnion([Q0])});
            skLineSegment(sketch, "E79", {"start": v(0, 74.25) * mm, "end": v(0, 104.25) * mm});
            skCircle(sketch, "E80", {"center": v(0, 104.25) * mm, "radius": 7.5 * mm});
            skArc(sketch, "E81", {"start": v(-15, 104.25) * mm, "mid": v(0.4, 119.24) * mm, "end": v(14.98, 103.44) * mm});
            skPoint(sketch, "E82.end.orphan", {"position": v(-58.2, 74.25) * mm});
            skLineSegment(sketch, "E83", {"start": v(-15, 104.25) * mm, "end": v(-15, 92.25) * mm});
            skLineSegment(sketch, "E84", {"start": v(-15, 92.25) * mm, "end": v(-33, 74.25) * mm});
            skLineSegment(sketch, "E85", {"start": v(14.98, 103.44) * mm, "end": v(14.98, 92.25) * mm});
            skLineSegment(sketch, "E86", {"start": v(14.98, 92.25) * mm, "end": v(32.98, 74.25) * mm});
            skLineSegment(sketch, "E87", {"start": v(74.25, 0) * mm, "end": v(-89.46, 0) * mm, "construction": true});
            skLineSegment(sketch, "E88.MirrorCS", {"start": v(-15, -92.25) * mm, "end": v(-33, -74.25) * mm});
            skLineSegment(sketch, "E89.MirrorCS", {"start": v(14.98, -92.25) * mm, "end": v(32.98, -74.25) * mm});
            skLineSegment(sketch, "E90.MirrorCS", {"start": v(-15, -104.25) * mm, "end": v(-15, -92.25) * mm});
            skLineSegment(sketch, "E91.MirrorCS", {"start": v(14.98, -103.44) * mm, "end": v(14.98, -92.25) * mm});
            skArc(sketch, "E92.MirrorCS", {"start": v(-15, -104.25) * mm, "mid": v(0.4, -119.24) * mm, "end": v(14.98, -103.44) * mm});
            skCircle(sketch, "E93.MirrorC", {"center": v(0, -104.25) * mm, "radius": 7.5 * mm});
            skSolve(sketch);
        }
        {
            var Q0;
            Q0=makeQuery(id+"F16.imprint","IMPRINT",FACE,{"disambiguationData":[TD([[makeQuery(id+"F16.imprint","IMPRINT",EDGE,{"derivedFrom":makeQuery(id+"F1.opExtrude","CAP_EDGE",EDGE,{"disambiguationData":[OSD([sQuery(id+"F0.wireOp",EDGE,"E1.left")])],"isStart":true})}),-1.0]])]});
            var Q1;
            Q1=makeQuery(id+"F16.imprint","IMPRINT",FACE,{"disambiguationData":[TD([[makeQuery(id+"F16.imprint","IMPRINT",EDGE,{"derivedFrom":sQuery(id+"F16.wireOp",EDGE,"E80")}),-1.0]])]});
            var Q2;
            {var subQ1=sQuery(id+"F16.wireOp",EDGE,"E88.MirrorCS");Q2=makeQuery(id+"F16.imprint","IMPRINT",FACE,{"disambiguationData":[TD([[makeQuery(id+"F16.imprint","IMPRINT",EDGE,{"derivedFrom":subQ1}),-1.0]])]});}
            var Q3;
            Q3=makeQuery(id+"F2.opExtrude","CAP_FACE",FACE,{"disambiguationData":[OSD([sQuery(id+"F0.wireOp",EDGE,"E12"),sQuery(id+"F0.wireOp",EDGE,"E13"),sQuery(id+"F0.wireOp",EDGE,"E14"),sQuery(id+"F0.wireOp",EDGE,"E15"),sQuery(id+"F0.wireOp",EDGE,"E17.filletArc"),sQuery(id+"F0.wireOp",EDGE,"E18.filletArc"),sQuery(id+"F0.wireOp",EDGE,"E19.filletArc"),sQuery(id+"F0.wireOp",EDGE,"E20.filletArc"),sQuery(id+"F0.wireOp",EDGE,"E25.0"),sQuery(id+"F0.wireOp",EDGE,"E25.1"),sQuery(id+"F0.wireOp",EDGE,"E25.2"),sQuery(id+"F0.wireOp",EDGE,"E25.3"),sQuery(id+"F0.wireOp",EDGE,"E25.4"),sQuery(id+"F0.wireOp",EDGE,"E25.5"),sQuery(id+"F0.wireOp",EDGE,"E25.6"),sQuery(id+"F0.wireOp",EDGE,"E25.7")])],"isStart":false});
            extrude(context, id + "F17", {"entities" : qUnion([Q0, Q1, Q2]), "endBound" : BoundingType.UP_TO_SURFACE, "depth" : 25.4 * mm, "endBoundEntityFace" : qUnion([Q3]), "offsetDistance" : 25.4 * mm});
        }
    });
